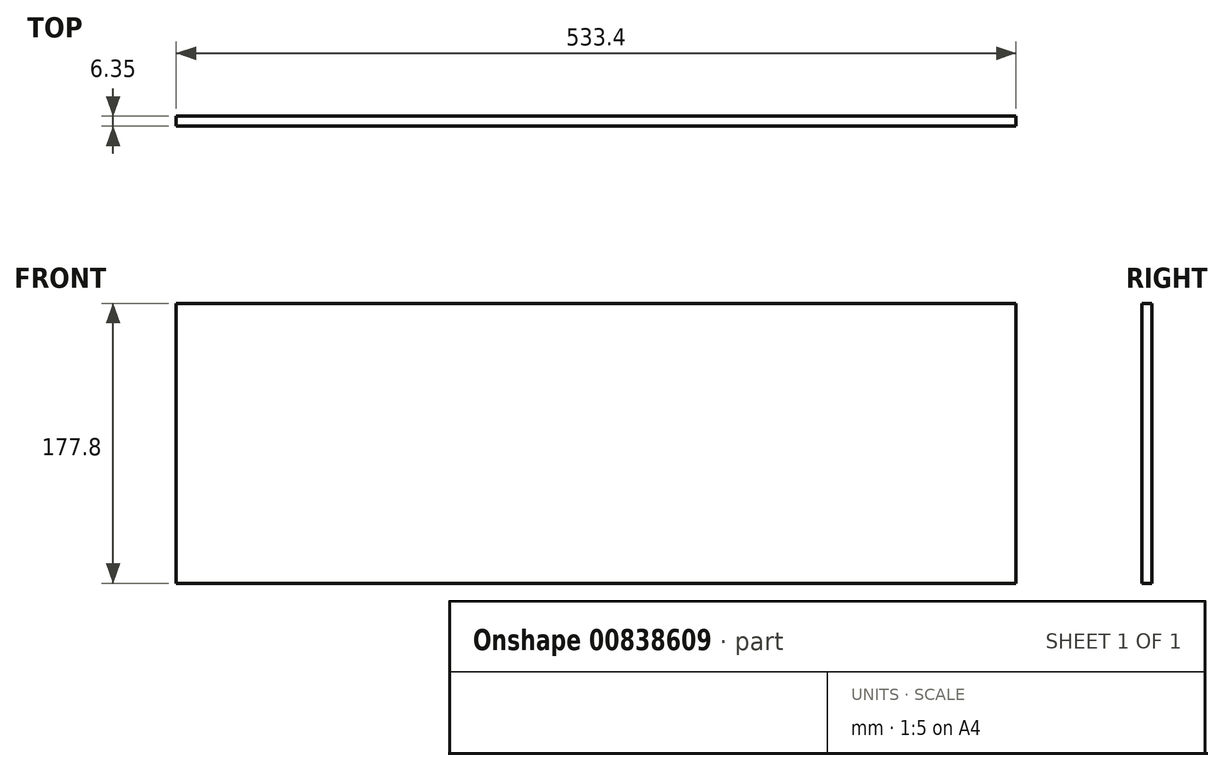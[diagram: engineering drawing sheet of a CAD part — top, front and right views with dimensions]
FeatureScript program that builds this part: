
annotation { "Feature Type Name" : "Feature", "Feature Type Description" : "" }
export const myFeature = defineFeature(function(context is Context, id is Id, definition is map)
    precondition{}
    {
        {
            var Q0;
            Q0=qCreatedBy(makeId("Front.planeOp"),FACE);
            var sketch = newSketch(context, id + "F0", { "sketchPlane" : qUnion([Q0])});
            skLineSegment(sketch, "E0.bottom", {"start": v(-290.57, 64.03) * mm, "end": v(242.83, 64.03) * mm});
            skLineSegment(sketch, "E0.top", {"start": v(-290.57, -113.77) * mm, "end": v(242.83, -113.77) * mm});
            skLineSegment(sketch, "E0.left", {"start": v(-290.57, 64.03) * mm, "end": v(-290.57, -113.77) * mm});
            skLineSegment(sketch, "E0.right", {"start": v(242.83, 64.03) * mm, "end": v(242.83, -113.77) * mm});
            skSolve(sketch);
        }
        {
            var Q0;
            Q0=makeQuery(id+"F0.imprint","IMPRINT",FACE,{"disambiguationData":[TD([[makeQuery(id+"F0.imprint","IMPRINT",EDGE,{"derivedFrom":sQuery(id+"F0.wireOp",EDGE,"E0.bottom")}),-1.0]])]});
            extrude(context, id + "F1", {"entities" : qUnion([Q0]), "depth" : 6.35 * mm, "offsetDistance" : 25.4 * mm});
        }
    });
